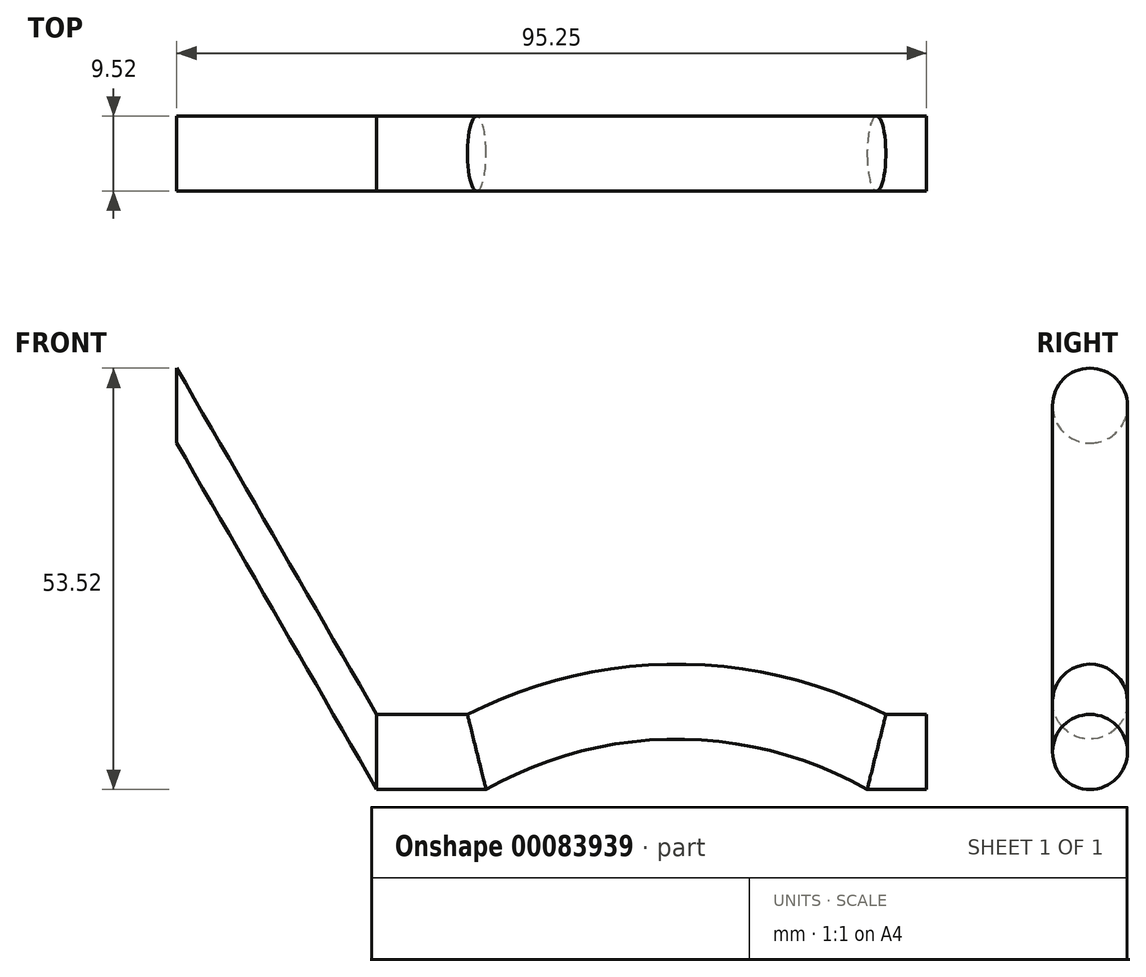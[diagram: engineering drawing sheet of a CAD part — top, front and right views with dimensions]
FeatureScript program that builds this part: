
annotation { "Feature Type Name" : "Feature", "Feature Type Description" : "" }
export const myFeature = defineFeature(function(context is Context, id is Id, definition is map)
    precondition{}
    {
        {
            var Q0;
            Q0=qCreatedBy(makeId("Right.planeOp"),FACE);
            var sketch = newSketch(context, id + "F0", { "sketchPlane" : qUnion([Q0])});
            skCircle(sketch, "E0", {"center": v(0, 0) * mm, "radius": 4.76 * mm});
            skSolve(sketch);
        }
        {
            var Q0;
            Q0=qCreatedBy(makeId("Front.planeOp"),FACE);
            var sketch = newSketch(context, id + "F1", { "sketchPlane" : qUnion([Q0])});
            skLineSegment(sketch, "E1", {"start": v(12.7, 0) * mm, "end": v(63.5, 0) * mm});
            skArc(sketch, "E2", {"start": v(63.5, 0) * mm, "mid": v(38.1, 6.4) * mm, "end": v(12.7, 0) * mm});
            skLineSegment(sketch, "E3", {"start": v(63.5, 0) * mm, "end": v(69.85, 0) * mm});
            skLineSegment(sketch, "E4", {"start": v(12.7, 0) * mm, "end": v(0, 0) * mm});
            skSolve(sketch);
        }
        {
            var Q0;
            Q0=makeQuery(id+"F0.imprint","IMPRINT",FACE,{"disambiguationData":[TD([[makeQuery(id+"F0.imprint","IMPRINT",EDGE,{"derivedFrom":sQuery(id+"F0.wireOp",EDGE,"E0")}),1.0]])]});
            var Q1;
            Q1=sQuery(id+"F1.wireOp",EDGE,"E4");
            var Q2;
            Q2=sQuery(id+"F1.wireOp",EDGE,"E2");
            var Q3;
            Q3=sQuery(id+"F1.wireOp",EDGE,"E3");
            sweep(context, id + "F2", {"profiles" : qUnion([Q0]), "path" : qUnion([Q1, Q2, Q3])});
        }
        {
            var Q0;
            Q0=qCreatedBy(makeId("Front.planeOp"),FACE);
            var sketch = newSketch(context, id + "F3", { "sketchPlane" : qUnion([Q0])});
            skLineSegment(sketch, "E5", {"start": v(0, 0) * mm, "end": v(-6.35, 0) * mm});
            skLineSegment(sketch, "E6", {"start": v(-6.35, 0) * mm, "end": v(-31.75, 44) * mm});
            skSolve(sketch);
        }
        {
            var Q0;
            Q0=makeQuery(id+"F2.opSweep","CAP_FACE",FACE,{"disambiguationData":[OSD([sQuery(id+"F0.wireOp",EDGE,"E0"),sQuery(id+"F1.wireOp",VERTEX,"E4.end")])],"isStart":true});
            var Q1;
            Q1=sQuery(id+"F3.wireOp",EDGE,"E6");
            sweep(context, id + "F4", {"operationType" : NewBodyOperationType.ADD, "profiles" : qUnion([Q0]), "path" : qUnion([Q1])});
        }
    });
